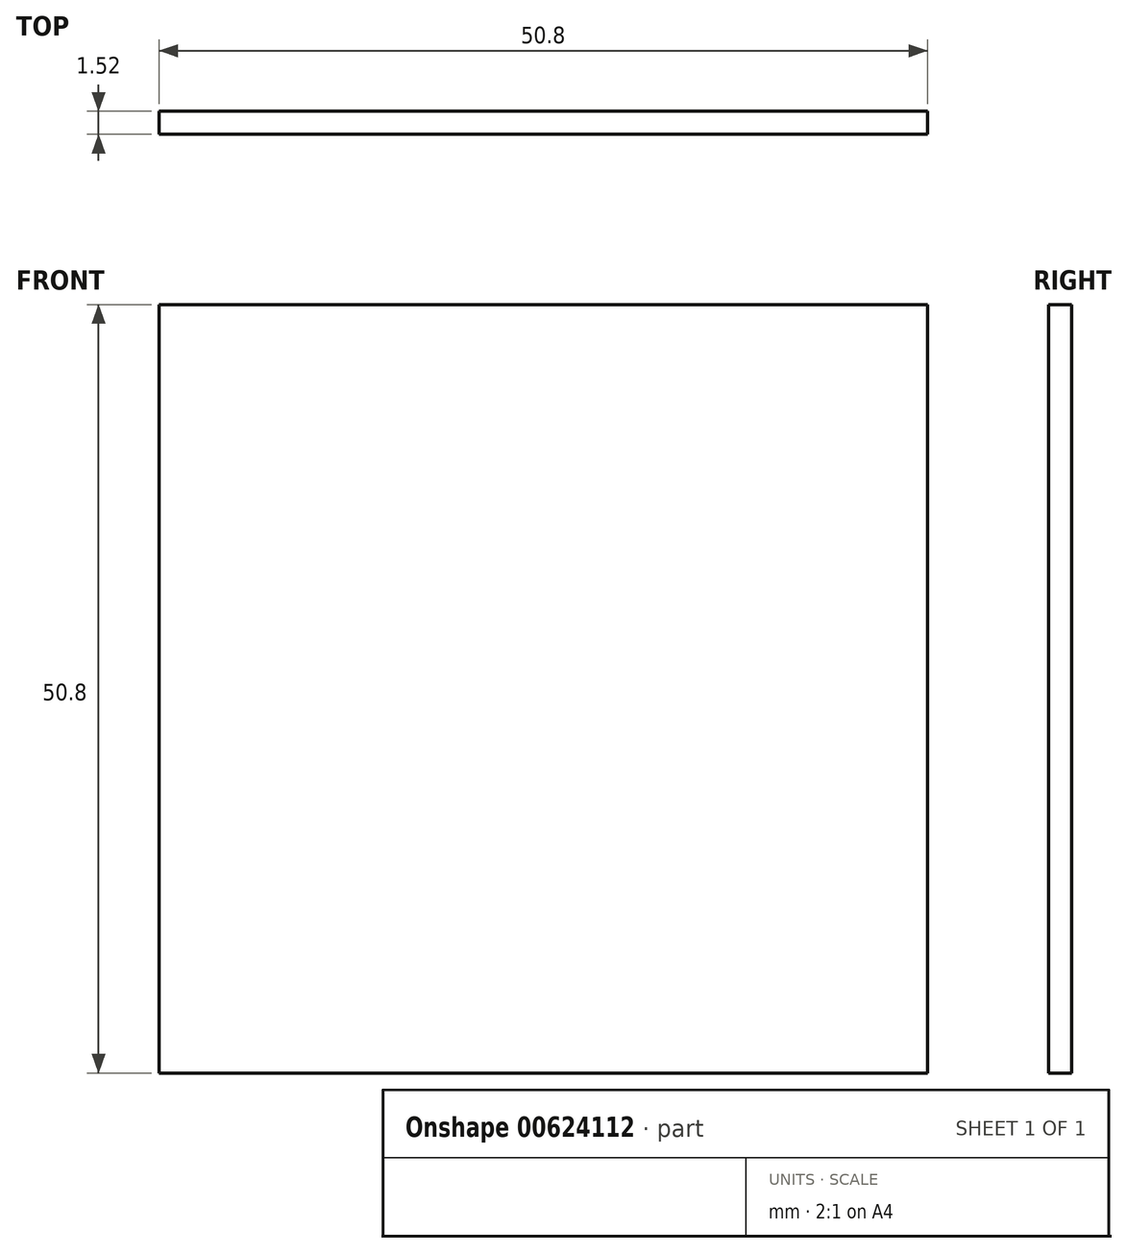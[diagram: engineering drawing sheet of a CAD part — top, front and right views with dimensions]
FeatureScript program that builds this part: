
annotation { "Feature Type Name" : "Feature", "Feature Type Description" : "" }
export const myFeature = defineFeature(function(context is Context, id is Id, definition is map)
    precondition{}
    {
        {
            var Q0;
            Q0=qCreatedBy(makeId("Front.planeOp"),FACE);
            var sketch = newSketch(context, id + "F0", { "sketchPlane" : qUnion([Q0])});
            skLineSegment(sketch, "E0.bottom", {"start": v(-83.11, 62.2) * mm, "end": v(-32.31, 62.2) * mm});
            skLineSegment(sketch, "E0.top", {"start": v(-83.11, 11.4) * mm, "end": v(-32.31, 11.4) * mm});
            skLineSegment(sketch, "E0.left", {"start": v(-83.11, 62.2) * mm, "end": v(-83.11, 11.4) * mm});
            skLineSegment(sketch, "E0.right", {"start": v(-32.31, 62.2) * mm, "end": v(-32.31, 11.4) * mm});
            skSolve(sketch);
        }
        {
            var Q0;
            Q0 = qSketchRegion(id + "F0", true);
            extrude(context, id + "F1", {"entities" : qUnion([Q0]), "endBound" : BoundingType.SYMMETRIC, "depth" : 1.52 * mm, "offsetDistance" : 25.4 * mm});
        }
    });
